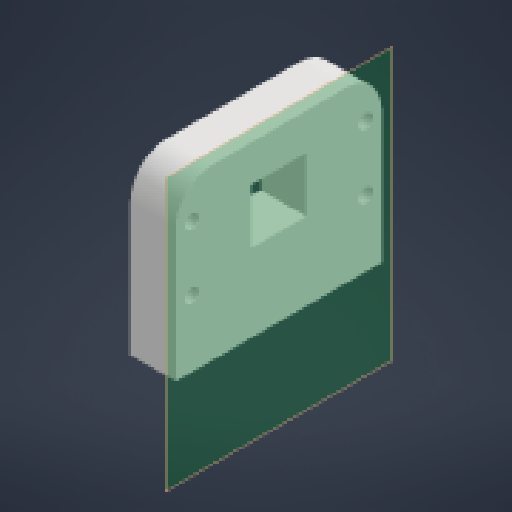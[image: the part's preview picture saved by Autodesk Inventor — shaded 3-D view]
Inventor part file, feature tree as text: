
AUTODESK INVENTOR PART (.ipt)
format: ipt  version: 2024 (Build 280153000, 153)  size: 157,696 bytes
history: native  units: mm
features: reference x17, other x7, extrude x2, sketch x2
ambient origin geometry x8: Origin, YZ Plane, XZ Plane, XY Plane, X Axis, Y Axis, Z Axis, Center Point
bodies: Body1 (feature_tree)
feature tree (28):
  other  "Твердое тело1"
  other  "РабПлоскость1"
  extrude  "Выдавливание1"  Depth=2.0mm
  extrude  "Выдавливание2"  Depth=12.0mm
  sketch  "Эскиз1"
  reference  "Ссылка1"
  reference  "Ссылка2"
  reference  "Ссылка3"
  reference  "Ссылка4"
  reference  "Ссылка5"
  reference  "Ссылка6"
  reference  "Ссылка7"
  reference  "Ссылка8"
  reference  "Ссылка9"
  reference  "Ссылка10"
  reference  "Ссылка11"
  reference  "Ссылка12"
  reference  "Ссылка13"
  reference  "Ссылка14"
  reference  "Ссылка15"
  sketch  "Эскиз2"
  reference  "Ссылка16"
  reference  "Ссылка17"
  parser-record x1  (decoder bookkeeping rows leaked as tree rows — omitted from the tree; the rows remain in map.json)
  other  "manipulator.iam"
  other  "bushing_asm:1"
  other  "bushing:1"
  other  "servo_80kg:1"
note: 1 file-system path scrubbed to <path> (originals preserved in map.json)
